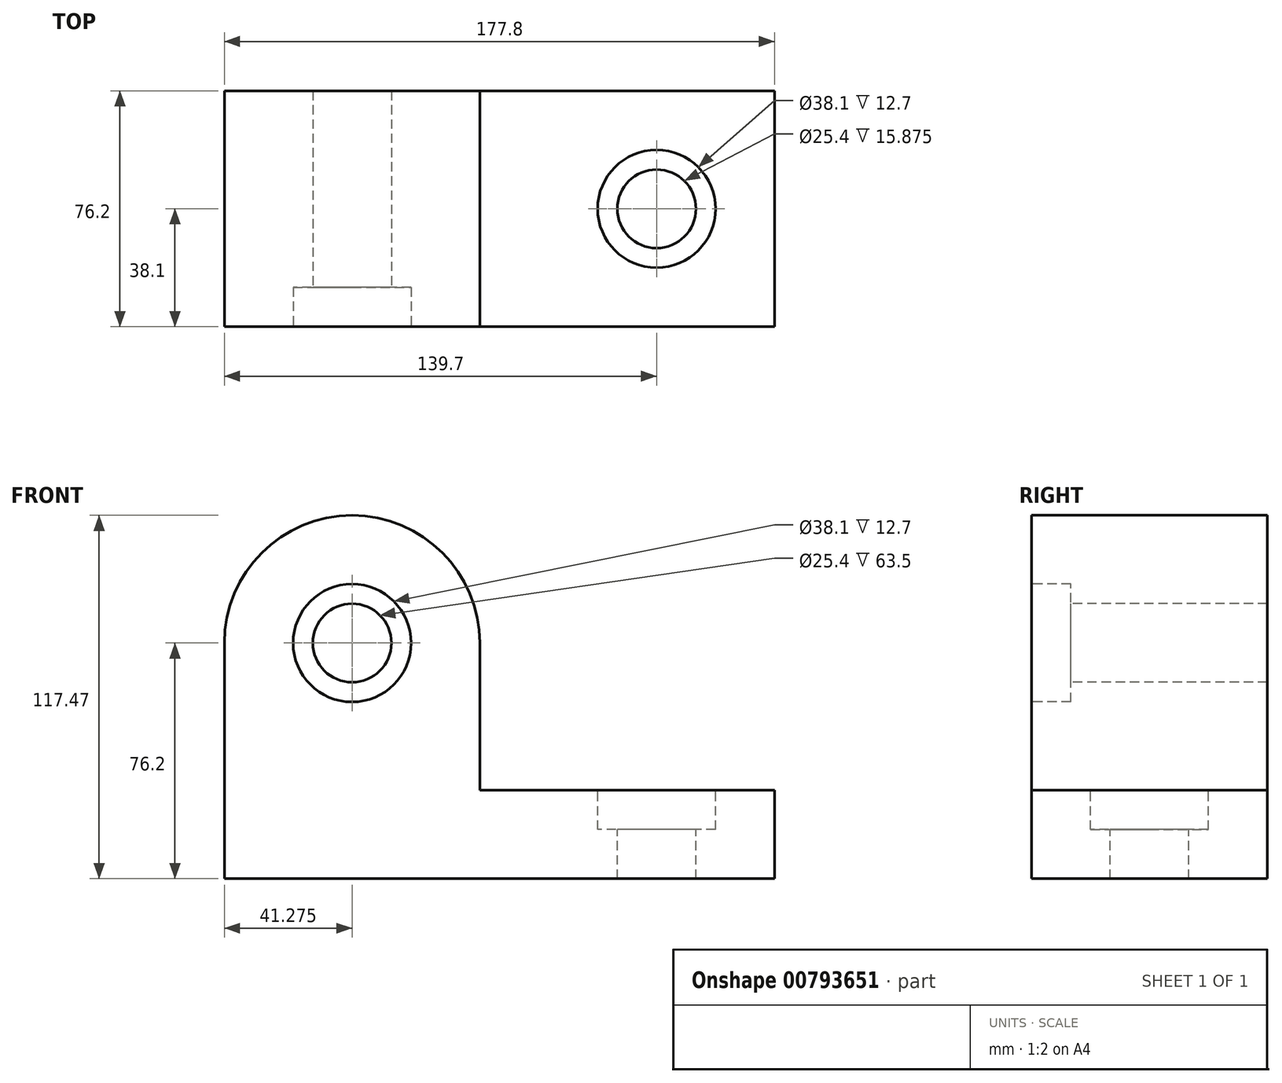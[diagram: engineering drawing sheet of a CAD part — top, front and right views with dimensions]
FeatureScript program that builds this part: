
annotation { "Feature Type Name" : "Feature", "Feature Type Description" : "" }
export const myFeature = defineFeature(function(context is Context, id is Id, definition is map)
    precondition{}
    {
        {
            var Q0;
            Q0=qCreatedBy(makeId("Front.planeOp"),FACE);
            var sketch = newSketch(context, id + "F0", { "sketchPlane" : qUnion([Q0])});
            skLineSegment(sketch, "E0", {"start": v(0, 0) * mm, "end": v(177.8, 0) * mm});
            skLineSegment(sketch, "E1", {"start": v(177.8, 0) * mm, "end": v(177.8, 28.58) * mm});
            skLineSegment(sketch, "E2", {"start": v(177.8, 28.58) * mm, "end": v(82.55, 28.58) * mm});
            skLineSegment(sketch, "E3", {"start": v(0, 0) * mm, "end": v(0, 127) * mm});
            skLineSegment(sketch, "E4", {"start": v(0, 127) * mm, "end": v(82.55, 127) * mm});
            skLineSegment(sketch, "E5", {"start": v(82.55, 127) * mm, "end": v(82.55, 28.58) * mm});
            skSolve(sketch);
        }
        {
            var Q0;
            Q0=makeQuery(id+"F0.imprint","IMPRINT",FACE,{"disambiguationData":[TD([[makeQuery(id+"F0.imprint","IMPRINT",EDGE,{"derivedFrom":sQuery(id+"F0.wireOp",EDGE,"E0")}),1.0]])]});
            extrude(context, id + "F1", {"entities" : qUnion([Q0]), "depth" : 76.2 * mm, "offsetDistance" : 25.4 * mm});
        }
        {
            var Q0;
            Q0=makeQuery(id+"F1.opExtrude","CAP_FACE",FACE,{"disambiguationData":[OSD([sQuery(id+"F0.wireOp",EDGE,"E0"),sQuery(id+"F0.wireOp",EDGE,"E1"),sQuery(id+"F0.wireOp",EDGE,"E2"),sQuery(id+"F0.wireOp",EDGE,"E3"),sQuery(id+"F0.wireOp",EDGE,"E4"),sQuery(id+"F0.wireOp",EDGE,"E5")])],"isStart":false});
            var sketch = newSketch(context, id + "F2", { "sketchPlane" : qUnion([Q0])});
            skLineSegment(sketch, "E6", {"start": v(0, 0) * mm, "end": v(0, 76.2) * mm, "construction": true});
            skLineSegment(sketch, "E7", {"start": v(0, 76.2) * mm, "end": v(41.28, 76.2) * mm, "construction": true});
            skArc(sketch, "E8", {"start": v(82.55, 76.2) * mm, "mid": v(41.27, 117.47) * mm, "end": v(0, 76.2) * mm});
            skSolve(sketch);
        }
        {
            var Q0;
            {var subQ0=sQuery(id+"F2.wireOp",EDGE,"E8");Q0=makeQuery(id+"F2.imprint","IMPRINT",FACE,{"disambiguationData":[TD([[makeQuery(id+"F2.imprint","IMPRINT",EDGE,{"derivedFrom":subQ0}),-1.0]])]});}
            extrude(context, id + "F3", {"entities" : qUnion([Q0]), "operationType" : NewBodyOperationType.REMOVE, "endBound" : BoundingType.THROUGH_ALL, "oppositeDirection" : true, "depth" : 25.4 * mm, "offsetDistance" : 25.4 * mm});
        }
        {
            var Q0;
            Q0=makeQuery(id+"F1.opExtrude","CAP_FACE",FACE,{"disambiguationData":[OSD([sQuery(id+"F0.wireOp",EDGE,"E0"),sQuery(id+"F0.wireOp",EDGE,"E1"),sQuery(id+"F0.wireOp",EDGE,"E2"),sQuery(id+"F0.wireOp",EDGE,"E3"),sQuery(id+"F0.wireOp",EDGE,"E4"),sQuery(id+"F0.wireOp",EDGE,"E5")])],"isStart":false});
            var sketch = newSketch(context, id + "F4", { "sketchPlane" : qUnion([Q0])});
            skLineSegment(sketch, "E9", {"start": v(0, 0) * mm, "end": v(0, 76.2) * mm, "construction": true});
            skLineSegment(sketch, "E10", {"start": v(0, 76.2) * mm, "end": v(41.28, 76.2) * mm, "construction": true});
            skCircle(sketch, "E11", {"center": v(41.28, 76.2) * mm, "radius": 19.05 * mm});
            skSolve(sketch);
        }
        {
            var Q0;
            Q0=makeQuery(id+"F4.imprint","IMPRINT",FACE,{"disambiguationData":[TD([[makeQuery(id+"F4.imprint","IMPRINT",EDGE,{"derivedFrom":sQuery(id+"F4.wireOp",EDGE,"E11")}),1.0]])]});
            extrude(context, id + "F5", {"entities" : qUnion([Q0]), "operationType" : NewBodyOperationType.REMOVE, "oppositeDirection" : true, "depth" : 12.7 * mm, "offsetDistance" : 25.4 * mm});
        }
        {
            var Q0;
            Q0=makeQuery(id+"F5.boolean.opBoolean","COPY",FACE,{"derivedFrom":makeQuery(id+"F5.opExtrude","CAP_FACE",FACE,{"disambiguationData":[OSD([sQuery(id+"F4.wireOp",EDGE,"E11")])],"isStart":false})});
            var sketch = newSketch(context, id + "F6", { "sketchPlane" : qUnion([Q0])});
            skLineSegment(sketch, "E12", {"start": v(22.23, 75.94) * mm, "end": v(41.28, 76.2) * mm, "construction": true});
            skCircle(sketch, "E13", {"center": v(41.28, 76.2) * mm, "radius": 12.7 * mm});
            skSolve(sketch);
        }
        {
            var Q0;
            Q0=makeQuery(id+"F6.imprint","IMPRINT",FACE,{"disambiguationData":[TD([[makeQuery(id+"F6.imprint","IMPRINT",EDGE,{"derivedFrom":sQuery(id+"F6.wireOp",EDGE,"E13")}),1.0]])]});
            extrude(context, id + "F7", {"entities" : qUnion([Q0]), "operationType" : NewBodyOperationType.REMOVE, "endBound" : BoundingType.THROUGH_ALL, "oppositeDirection" : true, "depth" : 25.4 * mm, "offsetDistance" : 25.4 * mm});
        }
        {
            var Q0;
            Q0=makeQuery(id+"F1.opExtrude","SWEPT_FACE",FACE,{"disambiguationData":[OSD([sQuery(id+"F0.wireOp",EDGE,"E2")])]});
            var sketch = newSketch(context, id + "F8", { "sketchPlane" : qUnion([Q0])});
            skLineSegment(sketch, "E14", {"start": v(177.8, -76.2) * mm, "end": v(177.8, -38.1) * mm, "construction": true});
            skLineSegment(sketch, "E15", {"start": v(177.8, -38.1) * mm, "end": v(139.7, -38.1) * mm, "construction": true});
            skCircle(sketch, "E16", {"center": v(139.7, -38.1) * mm, "radius": 19.05 * mm});
            skSolve(sketch);
        }
        {
            var Q0;
            Q0=makeQuery(id+"F8.imprint","IMPRINT",FACE,{"disambiguationData":[TD([[makeQuery(id+"F8.imprint","IMPRINT",EDGE,{"derivedFrom":sQuery(id+"F8.wireOp",EDGE,"E16")}),1.0]])]});
            extrude(context, id + "F9", {"entities" : qUnion([Q0]), "operationType" : NewBodyOperationType.REMOVE, "oppositeDirection" : true, "depth" : 12.7 * mm, "offsetDistance" : 25.4 * mm});
        }
        {
            var Q0;
            Q0=makeQuery(id+"F9.boolean.opBoolean","COPY",FACE,{"derivedFrom":makeQuery(id+"F9.opExtrude","CAP_FACE",FACE,{"disambiguationData":[OSD([sQuery(id+"F8.wireOp",EDGE,"E16")])],"isStart":false})});
            var sketch = newSketch(context, id + "F10", { "sketchPlane" : qUnion([Q0])});
            skLineSegment(sketch, "E17", {"start": v(120.73, -39.83) * mm, "end": v(139.7, -38.1) * mm, "construction": true});
            skCircle(sketch, "E18", {"center": v(139.7, -38.1) * mm, "radius": 12.7 * mm});
            skSolve(sketch);
        }
        {
            var Q0;
            Q0=makeQuery(id+"F10.imprint","IMPRINT",FACE,{"disambiguationData":[TD([[makeQuery(id+"F10.imprint","IMPRINT",EDGE,{"derivedFrom":sQuery(id+"F10.wireOp",EDGE,"E18")}),1.0]])]});
            extrude(context, id + "F11", {"entities" : qUnion([Q0]), "operationType" : NewBodyOperationType.REMOVE, "endBound" : BoundingType.THROUGH_ALL, "oppositeDirection" : true, "depth" : 25.4 * mm, "offsetDistance" : 25.4 * mm});
        }
    });
